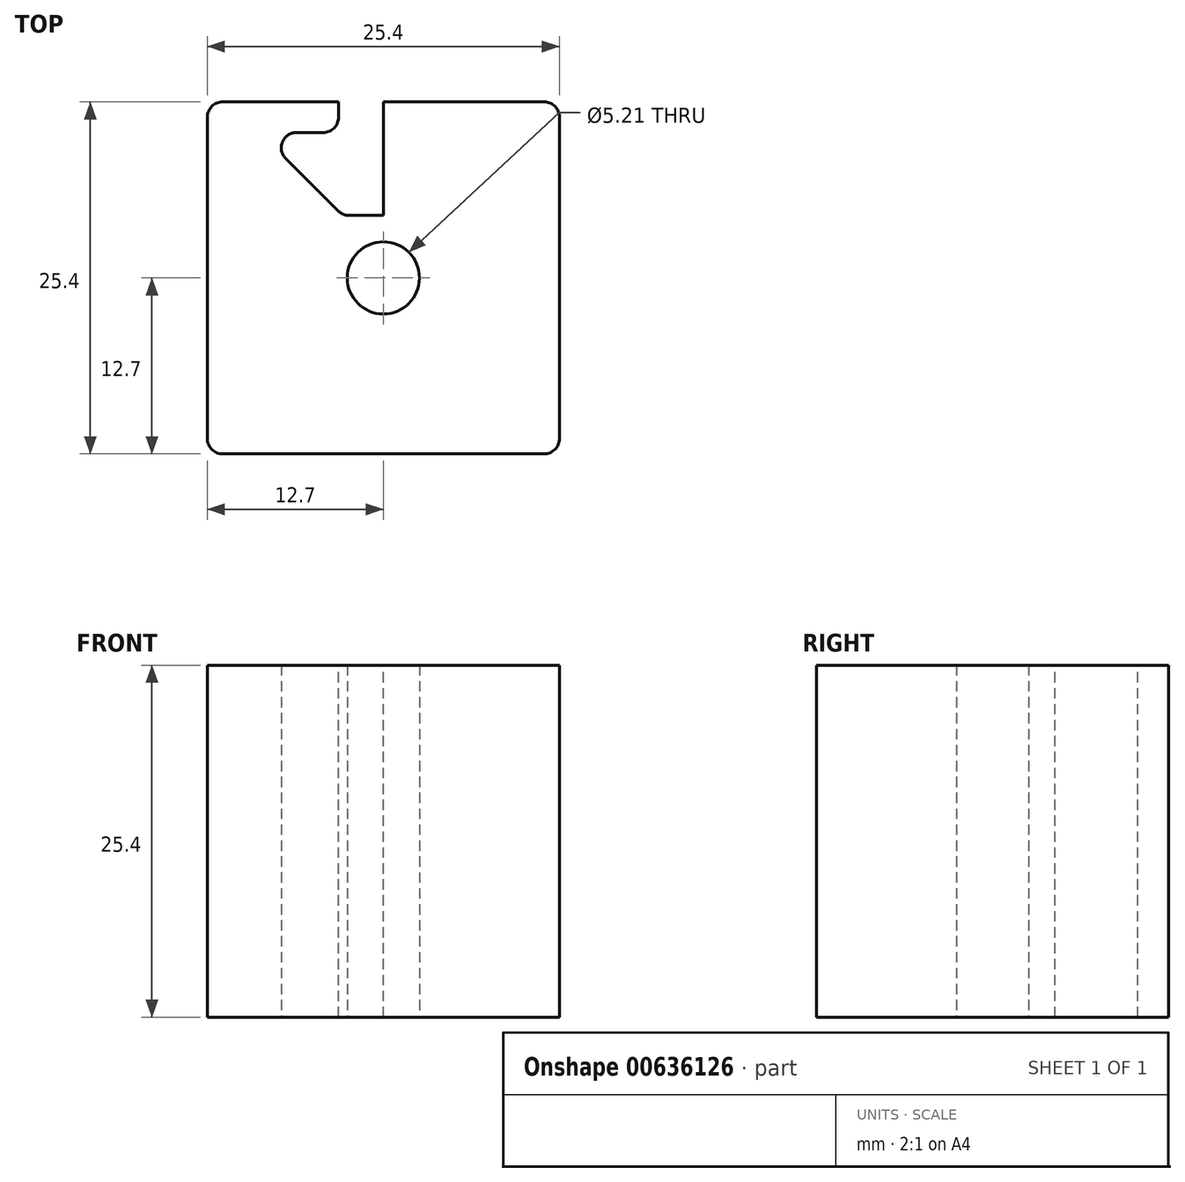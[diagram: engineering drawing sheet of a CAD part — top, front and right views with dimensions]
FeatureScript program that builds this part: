
annotation { "Feature Type Name" : "Feature", "Feature Type Description" : "" }
export const myFeature = defineFeature(function(context is Context, id is Id, definition is map)
    precondition{}
    {
        {
            var Q0;
            Q0=qCreatedBy(makeId("Top.planeOp"),FACE);
            var sketch = newSketch(context, id + "F0", { "sketchPlane" : qUnion([Q0])});
            skLineSegment(sketch, "E0.bottom", {"start": v(-12.7, 12.7) * mm, "end": v(12.7, 12.7) * mm});
            skLineSegment(sketch, "E0.top", {"start": v(-12.7, -12.7) * mm, "end": v(12.7, -12.7) * mm});
            skLineSegment(sketch, "E0.left", {"start": v(-12.7, 12.7) * mm, "end": v(-12.7, -12.7) * mm});
            skLineSegment(sketch, "E0.right", {"start": v(12.7, 12.7) * mm, "end": v(12.7, -12.7) * mm});
            skPoint(sketch, "E0.middle", {"position": v(0, 0) * mm});
            skCircle(sketch, "E1", {"center": v(0, 0) * mm, "radius": 2.6 * mm});
            skSolve(sketch);
        }
        {
            var Q0;
            Q0=qSketchRegion(id+"F0",true);
            extrude(context, id + "F1", {"entities" : qUnion([Q0]), "depth" : 25.4 * mm, "offsetDistance" : 25.4 * mm});
        }
        {
            var Q0;
            Q0=makeQuery(id+"F1.opExtrude","CAP_FACE",FACE,{"disambiguationData":[OSD([sQuery(id+"F0.wireOp",EDGE,"E0.bottom"),sQuery(id+"F0.wireOp",EDGE,"E0.top"),sQuery(id+"F0.wireOp",EDGE,"E0.left"),sQuery(id+"F0.wireOp",EDGE,"E0.right"),sQuery(id+"F0.wireOp",EDGE,"E1")])],"isStart":false});
            var sketch = newSketch(context, id + "F2", { "sketchPlane" : qUnion([Q0])});
            skLineSegment(sketch, "E2", {"start": v(-12.7, 12.7) * mm, "end": v(12.7, -12.7) * mm, "construction": true});
            skLineSegment(sketch, "E3.bottom", {"start": v(-4.5, 4.5) * mm, "end": v(4.5, 4.5) * mm});
            skLineSegment(sketch, "E3.top", {"start": v(-4.5, -4.5) * mm, "end": v(4.5, -4.5) * mm});
            skLineSegment(sketch, "E3.left", {"start": v(-4.5, 4.5) * mm, "end": v(-4.5, -4.5) * mm});
            skLineSegment(sketch, "E3.right", {"start": v(4.5, 4.5) * mm, "end": v(4.5, -4.5) * mm});
            skPoint(sketch, "E3.middle", {"position": v(0, 0) * mm});
            skLineSegment(sketch, "E4", {"start": v(-2.95, 4.5) * mm, "end": v(-8.93, 10.5) * mm});
            skLineSegment(sketch, "E5", {"start": v(-8.93, 10.5) * mm, "end": v(-3.24, 10.5) * mm});
            skLineSegment(sketch, "E6", {"start": v(-3.24, 10.5) * mm, "end": v(-3.24, 12.7) * mm});
            skLineSegment(sketch, "E7", {"start": v(-3.24, 12.7) * mm, "end": v(0, 12.7) * mm});
            skLineSegment(sketch, "E8", {"start": v(0, 12.7) * mm, "end": v(0, 4.5) * mm});
            skSolve(sketch);
        }
        {
            var Q0;
            {var subQ0=sQuery(id+"F2.wireOp",EDGE,"E4");Q0=makeQuery(id+"F2.imprint","IMPRINT",FACE,{"disambiguationData":[TD([[makeQuery(id+"F2.imprint","IMPRINT",EDGE,{"derivedFrom":subQ0}),-1.0]])]});}
            extrude(context, id + "F3", {"entities" : qUnion([Q0]), "operationType" : NewBodyOperationType.REMOVE, "endBound" : BoundingType.THROUGH_ALL, "oppositeDirection" : true, "depth" : 25.4 * mm, "offsetDistance" : 25.4 * mm});
        }
        {
            var Q0;
            Q0=makeQuery(id+"F1.opExtrude","SWEPT_EDGE",EDGE,{"disambiguationData":[OSD([sQuery(id+"F0.wireOp",EDGE,"E0.bottom"),sQuery(id+"F0.wireOp",EDGE,"E0.left")])]});
            var Q1;
            Q1=makeQuery(id+"F8KPk8WaW4Cchg5_1.3.FqZtEu0w99tbaJH_1.1.F3.boolean.opBoolean","COPY",EDGE,{"derivedFrom":makeQuery(id+"F8KPk8WaW4Cchg5_1.3.FqZtEu0w99tbaJH_1.1.F3.opExtrude","SWEPT_EDGE",EDGE,{"disambiguationData":[OSD([sQuery(id+"F0.wireOp",EDGE,"E0.bottom"),sQuery(id+"F2.wireOp",EDGE,"E6"),sQuery(id+"F2.wireOp",EDGE,"E7")])]})});
            var Q2;
            Q2=makeQuery(id+"F8KPk8WaW4Cchg5_1.1.F3.boolean.opBoolean","COPY",EDGE,{"derivedFrom":makeQuery(id+"F8KPk8WaW4Cchg5_1.1.F3.opExtrude","SWEPT_EDGE",EDGE,{"disambiguationData":[OSD([sQuery(id+"F0.wireOp",EDGE,"E0.bottom"),sQuery(id+"F2.wireOp",EDGE,"E6"),sQuery(id+"F2.wireOp",EDGE,"E7")])]})});
            var Q3;
            Q3=makeQuery(id+"F8KPk8WaW4Cchg5_1.1.F3.boolean.opBoolean","COPY",EDGE,{"derivedFrom":makeQuery(id+"F8KPk8WaW4Cchg5_1.1.F3.opExtrude","SWEPT_EDGE",EDGE,{"disambiguationData":[OSD([sQuery(id+"F2.wireOp",EDGE,"E5"),sQuery(id+"F2.wireOp",EDGE,"E6")])]})});
            var Q4;
            Q4=makeQuery(id+"F1.opExtrude","SWEPT_EDGE",EDGE,{"disambiguationData":[OSD([sQuery(id+"F0.wireOp",EDGE,"E0.top"),sQuery(id+"F0.wireOp",EDGE,"E0.left")])]});
            var Q5;
            Q5=makeQuery(id+"F8KPk8WaW4Cchg5_1.2.FqZtEu0w99tbaJH_1.1.F3.boolean.opBoolean","COPY",EDGE,{"derivedFrom":makeQuery(id+"F8KPk8WaW4Cchg5_1.2.FqZtEu0w99tbaJH_1.1.F3.opExtrude","SWEPT_EDGE",EDGE,{"disambiguationData":[OSD([sQuery(id+"F2.wireOp",EDGE,"E5"),sQuery(id+"F2.wireOp",EDGE,"E6")])]})});
            var Q6;
            Q6=makeQuery(id+"F8KPk8WaW4Cchg5_1.2.F3.boolean.opBoolean","COPY",EDGE,{"derivedFrom":makeQuery(id+"F8KPk8WaW4Cchg5_1.2.F3.opExtrude","SWEPT_EDGE",EDGE,{"disambiguationData":[OSD([sQuery(id+"F2.wireOp",EDGE,"E5"),sQuery(id+"F2.wireOp",EDGE,"E6")])]})});
            var Q7;
            Q7=makeQuery(id+"F8KPk8WaW4Cchg5_1.2.F3.boolean.opBoolean","COPY",EDGE,{"derivedFrom":makeQuery(id+"F8KPk8WaW4Cchg5_1.2.F3.opExtrude","SWEPT_EDGE",EDGE,{"disambiguationData":[OSD([sQuery(id+"F0.wireOp",EDGE,"E0.bottom"),sQuery(id+"F2.wireOp",EDGE,"E6"),sQuery(id+"F2.wireOp",EDGE,"E7")])]})});
            var Q8;
            Q8=makeQuery(id+"F8KPk8WaW4Cchg5_1.1.FqZtEu0w99tbaJH_1.1.F3.boolean.opBoolean","COPY",EDGE,{"derivedFrom":makeQuery(id+"F8KPk8WaW4Cchg5_1.1.FqZtEu0w99tbaJH_1.1.F3.opExtrude","SWEPT_EDGE",EDGE,{"disambiguationData":[OSD([sQuery(id+"F2.wireOp",EDGE,"E5"),sQuery(id+"F2.wireOp",EDGE,"E6")])]})});
            var Q9;
            Q9=makeQuery(id+"F8KPk8WaW4Cchg5_1.1.FqZtEu0w99tbaJH_1.1.F3.boolean.opBoolean","COPY",EDGE,{"derivedFrom":makeQuery(id+"F8KPk8WaW4Cchg5_1.1.FqZtEu0w99tbaJH_1.1.F3.opExtrude","SWEPT_EDGE",EDGE,{"disambiguationData":[OSD([sQuery(id+"F0.wireOp",EDGE,"E0.bottom"),sQuery(id+"F2.wireOp",EDGE,"E6"),sQuery(id+"F2.wireOp",EDGE,"E7")])]})});
            var Q10;
            Q10=makeQuery(id+"F8KPk8WaW4Cchg5_1.1.FqZtEu0w99tbaJH_1.1.F3.boolean.opBoolean","COPY",EDGE,{"derivedFrom":makeQuery(id+"F8KPk8WaW4Cchg5_1.1.FqZtEu0w99tbaJH_1.1.F3.opExtrude","SWEPT_EDGE",EDGE,{"disambiguationData":[OSD([sQuery(id+"F2.wireOp",EDGE,"E4"),sQuery(id+"F2.wireOp",EDGE,"E5")])]})});
            var Q11;
            Q11=makeQuery(id+"F8KPk8WaW4Cchg5_1.3.F3.boolean.opBoolean","COPY",EDGE,{"derivedFrom":makeQuery(id+"F8KPk8WaW4Cchg5_1.3.F3.opExtrude","SWEPT_EDGE",EDGE,{"disambiguationData":[OSD([sQuery(id+"F2.wireOp",EDGE,"E5"),sQuery(id+"F2.wireOp",EDGE,"E6")])]})});
            var Q12;
            Q12=makeQuery(id+"FqZtEu0w99tbaJH_1.1.F3.boolean.opBoolean","COPY",EDGE,{"derivedFrom":makeQuery(id+"FqZtEu0w99tbaJH_1.1.F3.opExtrude","SWEPT_EDGE",EDGE,{"disambiguationData":[OSD([sQuery(id+"F2.wireOp",EDGE,"E5"),sQuery(id+"F2.wireOp",EDGE,"E6")])]})});
            var Q13;
            Q13=makeQuery(id+"F3.boolean.opBoolean","COPY",EDGE,{"derivedFrom":makeQuery(id+"F3.opExtrude","SWEPT_EDGE",EDGE,{"disambiguationData":[OSD([sQuery(id+"F0.wireOp",EDGE,"E0.bottom"),sQuery(id+"F2.wireOp",EDGE,"E6"),sQuery(id+"F2.wireOp",EDGE,"E7")])]})});
            var Q14;
            Q14=makeQuery(id+"F1.opExtrude","SWEPT_EDGE",EDGE,{"disambiguationData":[OSD([sQuery(id+"F0.wireOp",EDGE,"E0.bottom"),sQuery(id+"F0.wireOp",EDGE,"E0.right")])]});
            var Q15;
            Q15=makeQuery(id+"F3.boolean.opBoolean","COPY",EDGE,{"derivedFrom":makeQuery(id+"F3.opExtrude","SWEPT_EDGE",EDGE,{"disambiguationData":[OSD([sQuery(id+"F2.wireOp",EDGE,"E5"),sQuery(id+"F2.wireOp",EDGE,"E6")])]})});
            var Q16;
            Q16=makeQuery(id+"F8KPk8WaW4Cchg5_1.3.FqZtEu0w99tbaJH_1.1.F3.boolean.opBoolean","COPY",EDGE,{"derivedFrom":makeQuery(id+"F8KPk8WaW4Cchg5_1.3.FqZtEu0w99tbaJH_1.1.F3.opExtrude","SWEPT_EDGE",EDGE,{"disambiguationData":[OSD([sQuery(id+"F2.wireOp",EDGE,"E5"),sQuery(id+"F2.wireOp",EDGE,"E6")])]})});
            var Q17;
            Q17=makeQuery(id+"F8KPk8WaW4Cchg5_1.3.FqZtEu0w99tbaJH_1.1.F3.boolean.opBoolean","COPY",EDGE,{"derivedFrom":makeQuery(id+"F8KPk8WaW4Cchg5_1.3.FqZtEu0w99tbaJH_1.1.F3.opExtrude","SWEPT_EDGE",EDGE,{"disambiguationData":[OSD([sQuery(id+"F2.wireOp",EDGE,"E4"),sQuery(id+"F2.wireOp",EDGE,"E5")])]})});
            var Q18;
            Q18=makeQuery(id+"F8KPk8WaW4Cchg5_1.3.F3.boolean.opBoolean","COPY",EDGE,{"derivedFrom":makeQuery(id+"F8KPk8WaW4Cchg5_1.3.F3.opExtrude","SWEPT_EDGE",EDGE,{"disambiguationData":[OSD([sQuery(id+"F0.wireOp",EDGE,"E0.bottom"),sQuery(id+"F2.wireOp",EDGE,"E6"),sQuery(id+"F2.wireOp",EDGE,"E7")])]})});
            var Q19;
            Q19=makeQuery(id+"F8KPk8WaW4Cchg5_1.1.F3.boolean.opBoolean","COPY",EDGE,{"derivedFrom":makeQuery(id+"F8KPk8WaW4Cchg5_1.1.F3.opExtrude","SWEPT_EDGE",EDGE,{"disambiguationData":[OSD([sQuery(id+"F2.wireOp",EDGE,"E3.bottom"),sQuery(id+"F2.wireOp",EDGE,"E4")])]})});
            var Q20;
            Q20=makeQuery(id+"F8KPk8WaW4Cchg5_1.2.FqZtEu0w99tbaJH_1.1.F3.boolean.opBoolean","COPY",EDGE,{"derivedFrom":makeQuery(id+"F8KPk8WaW4Cchg5_1.2.FqZtEu0w99tbaJH_1.1.F3.opExtrude","SWEPT_EDGE",EDGE,{"disambiguationData":[OSD([sQuery(id+"F2.wireOp",EDGE,"E3.bottom"),sQuery(id+"F2.wireOp",EDGE,"E4")])]})});
            var Q21;
            Q21=makeQuery(id+"F8KPk8WaW4Cchg5_1.2.F3.boolean.opBoolean","COPY",EDGE,{"derivedFrom":makeQuery(id+"F8KPk8WaW4Cchg5_1.2.F3.opExtrude","SWEPT_EDGE",EDGE,{"disambiguationData":[OSD([sQuery(id+"F2.wireOp",EDGE,"E3.bottom"),sQuery(id+"F2.wireOp",EDGE,"E4")])]})});
            var Q22;
            Q22=makeQuery(id+"F8KPk8WaW4Cchg5_1.3.F3.boolean.opBoolean","COPY",EDGE,{"derivedFrom":makeQuery(id+"F8KPk8WaW4Cchg5_1.3.F3.opExtrude","SWEPT_EDGE",EDGE,{"disambiguationData":[OSD([sQuery(id+"F2.wireOp",EDGE,"E3.bottom"),sQuery(id+"F2.wireOp",EDGE,"E4")])]})});
            var Q23;
            Q23=makeQuery(id+"F8KPk8WaW4Cchg5_1.3.FqZtEu0w99tbaJH_1.1.F3.boolean.opBoolean","COPY",EDGE,{"derivedFrom":makeQuery(id+"F8KPk8WaW4Cchg5_1.3.FqZtEu0w99tbaJH_1.1.F3.opExtrude","SWEPT_EDGE",EDGE,{"disambiguationData":[OSD([sQuery(id+"F2.wireOp",EDGE,"E3.bottom"),sQuery(id+"F2.wireOp",EDGE,"E4")])]})});
            var Q24;
            Q24=makeQuery(id+"F8KPk8WaW4Cchg5_1.1.FqZtEu0w99tbaJH_1.1.F3.boolean.opBoolean","COPY",EDGE,{"derivedFrom":makeQuery(id+"F8KPk8WaW4Cchg5_1.1.FqZtEu0w99tbaJH_1.1.F3.opExtrude","SWEPT_EDGE",EDGE,{"disambiguationData":[OSD([sQuery(id+"F2.wireOp",EDGE,"E3.bottom"),sQuery(id+"F2.wireOp",EDGE,"E4")])]})});
            var Q25;
            Q25=makeQuery(id+"F8KPk8WaW4Cchg5_1.2.FqZtEu0w99tbaJH_1.1.F3.boolean.opBoolean","COPY",EDGE,{"derivedFrom":makeQuery(id+"F8KPk8WaW4Cchg5_1.2.FqZtEu0w99tbaJH_1.1.F3.opExtrude","SWEPT_EDGE",EDGE,{"disambiguationData":[OSD([sQuery(id+"F2.wireOp",EDGE,"E4"),sQuery(id+"F2.wireOp",EDGE,"E5")])]})});
            var Q26;
            Q26=makeQuery(id+"F8KPk8WaW4Cchg5_1.1.F3.boolean.opBoolean","COPY",EDGE,{"derivedFrom":makeQuery(id+"F8KPk8WaW4Cchg5_1.1.F3.opExtrude","SWEPT_EDGE",EDGE,{"disambiguationData":[OSD([sQuery(id+"F2.wireOp",EDGE,"E4"),sQuery(id+"F2.wireOp",EDGE,"E5")])]})});
            var Q27;
            Q27=makeQuery(id+"F8KPk8WaW4Cchg5_1.2.F3.boolean.opBoolean","COPY",EDGE,{"derivedFrom":makeQuery(id+"F8KPk8WaW4Cchg5_1.2.F3.opExtrude","SWEPT_EDGE",EDGE,{"disambiguationData":[OSD([sQuery(id+"F2.wireOp",EDGE,"E4"),sQuery(id+"F2.wireOp",EDGE,"E5")])]})});
            var Q28;
            Q28=makeQuery(id+"F8KPk8WaW4Cchg5_1.2.FqZtEu0w99tbaJH_1.1.F3.boolean.opBoolean","COPY",EDGE,{"derivedFrom":makeQuery(id+"F8KPk8WaW4Cchg5_1.2.FqZtEu0w99tbaJH_1.1.F3.opExtrude","SWEPT_EDGE",EDGE,{"disambiguationData":[OSD([sQuery(id+"F0.wireOp",EDGE,"E0.bottom"),sQuery(id+"F2.wireOp",EDGE,"E6"),sQuery(id+"F2.wireOp",EDGE,"E7")])]})});
            var Q29;
            Q29=makeQuery(id+"F1.opExtrude","SWEPT_EDGE",EDGE,{"disambiguationData":[OSD([sQuery(id+"F0.wireOp",EDGE,"E0.top"),sQuery(id+"F0.wireOp",EDGE,"E0.right")])]});
            var Q30;
            Q30=makeQuery(id+"F8KPk8WaW4Cchg5_1.3.F3.boolean.opBoolean","COPY",EDGE,{"derivedFrom":makeQuery(id+"F8KPk8WaW4Cchg5_1.3.F3.opExtrude","SWEPT_EDGE",EDGE,{"disambiguationData":[OSD([sQuery(id+"F2.wireOp",EDGE,"E4"),sQuery(id+"F2.wireOp",EDGE,"E5")])]})});
            var Q31;
            Q31=makeQuery(id+"FqZtEu0w99tbaJH_1.1.F3.boolean.opBoolean","COPY",EDGE,{"derivedFrom":makeQuery(id+"FqZtEu0w99tbaJH_1.1.F3.opExtrude","SWEPT_EDGE",EDGE,{"disambiguationData":[OSD([sQuery(id+"F2.wireOp",EDGE,"E4"),sQuery(id+"F2.wireOp",EDGE,"E5")])]})});
            var Q32;
            Q32=makeQuery(id+"F3.boolean.opBoolean","COPY",EDGE,{"derivedFrom":makeQuery(id+"F3.opExtrude","SWEPT_EDGE",EDGE,{"disambiguationData":[OSD([sQuery(id+"F2.wireOp",EDGE,"E4"),sQuery(id+"F2.wireOp",EDGE,"E5")])]})});
            var Q33;
            Q33=makeQuery(id+"F3.boolean.opBoolean","COPY",EDGE,{"derivedFrom":makeQuery(id+"F3.opExtrude","SWEPT_EDGE",EDGE,{"disambiguationData":[OSD([sQuery(id+"F2.wireOp",EDGE,"E3.bottom"),sQuery(id+"F2.wireOp",EDGE,"E4")])]})});
            var Q34;
            Q34=makeQuery(id+"FqZtEu0w99tbaJH_1.1.F3.boolean.opBoolean","COPY",EDGE,{"derivedFrom":makeQuery(id+"FqZtEu0w99tbaJH_1.1.F3.opExtrude","SWEPT_EDGE",EDGE,{"disambiguationData":[OSD([sQuery(id+"F2.wireOp",EDGE,"E3.bottom"),sQuery(id+"F2.wireOp",EDGE,"E4")])]})});
            var Q35;
            Q35=makeQuery(id+"FqZtEu0w99tbaJH_1.1.F3.boolean.opBoolean","COPY",EDGE,{"derivedFrom":makeQuery(id+"FqZtEu0w99tbaJH_1.1.F3.opExtrude","SWEPT_EDGE",EDGE,{"disambiguationData":[OSD([sQuery(id+"F0.wireOp",EDGE,"E0.bottom"),sQuery(id+"F2.wireOp",EDGE,"E6"),sQuery(id+"F2.wireOp",EDGE,"E7")])]})});
            fillet(context, id + "F4", {"entities" : qUnion([Q0, Q1, Q2, Q3, Q4, Q5, Q6, Q7, Q8, Q9, Q10, Q11, Q12, Q13, Q14, Q15, Q16, Q17, Q18, Q19, Q20, Q21, Q22, Q23, Q24, Q25, Q26, Q27, Q28, Q29, Q30, Q31, Q32, Q33, Q34, Q35]), "radius" : 1.1 * mm, "tangentPropagation" : true, "allowEdgeOverflow" : false});
        }
    });
